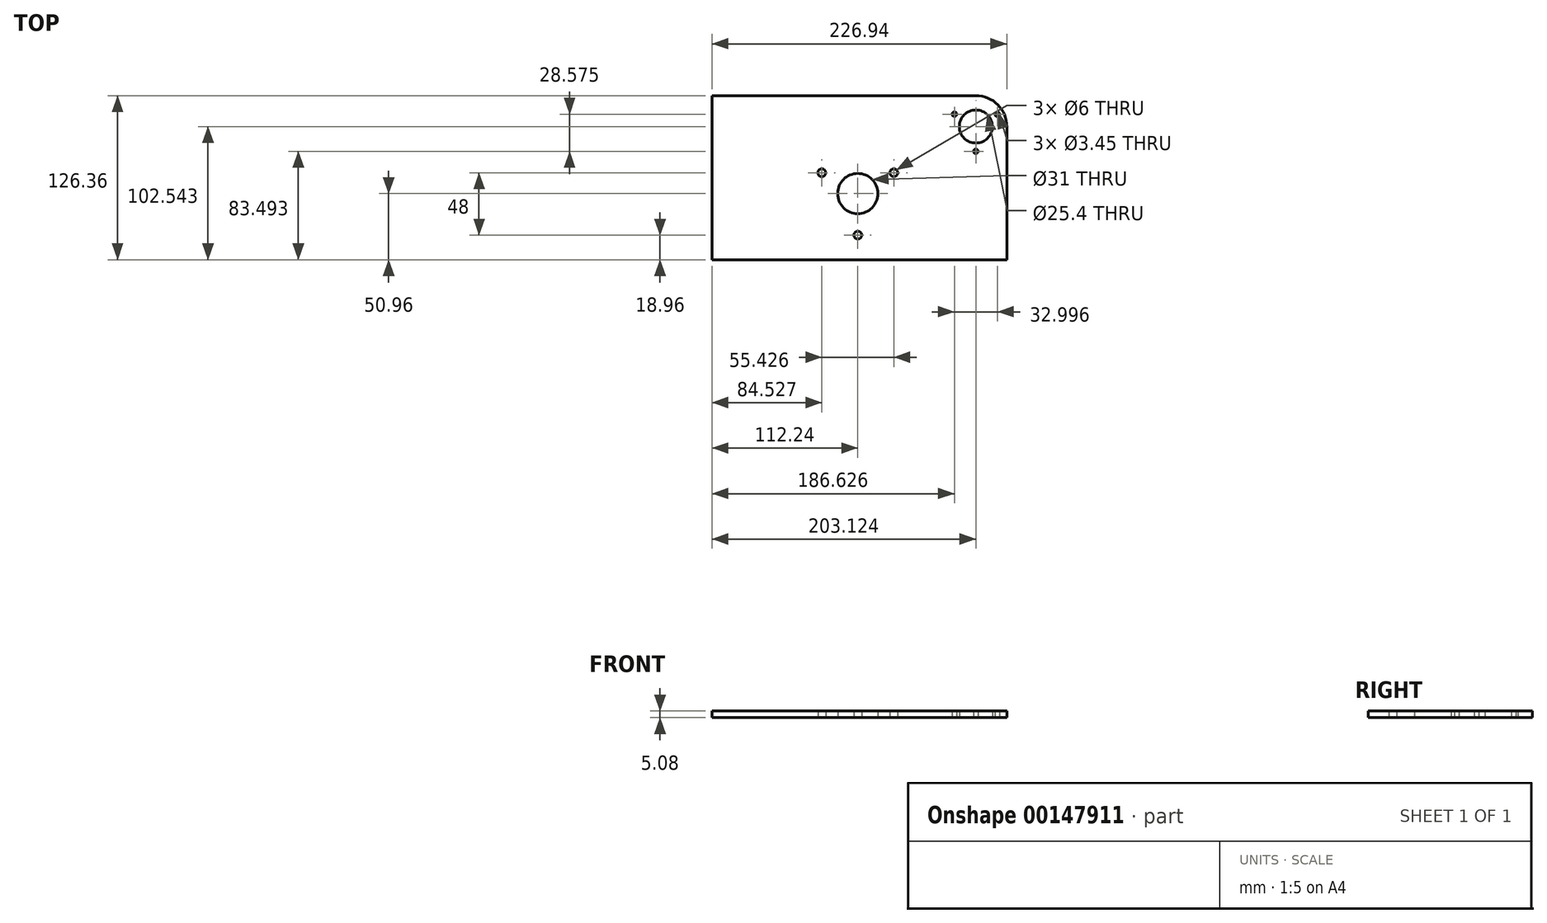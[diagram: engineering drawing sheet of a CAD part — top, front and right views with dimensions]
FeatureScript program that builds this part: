
annotation { "Feature Type Name" : "Feature", "Feature Type Description" : "" }
export const myFeature = defineFeature(function(context is Context, id is Id, definition is map)
    precondition{}
    {
        {
            var Q0;
            Q0=qCreatedBy(makeId("Top.planeOp"),FACE);
            var sketch = newSketch(context, id + "F0", { "sketchPlane" : qUnion([Q0])});
            skLineSegment(sketch, "E0", {"start": v(0, 0) * mm, "end": v(0, -32) * mm, "construction": true});
            skLineSegment(sketch, "E1", {"start": v(0, 0) * mm, "end": v(-27.71, 16) * mm, "construction": true});
            skLineSegment(sketch, "E2", {"start": v(0, 0) * mm, "end": v(27.71, 16) * mm, "construction": true});
            skLineSegment(sketch, "E3", {"start": v(0, -32) * mm, "end": v(-27.71, 16) * mm, "construction": true});
            skLineSegment(sketch, "E4", {"start": v(-27.71, 16) * mm, "end": v(27.71, 16) * mm, "construction": true});
            skLineSegment(sketch, "E5", {"start": v(27.71, 16) * mm, "end": v(0, -32) * mm, "construction": true});
            skCircle(sketch, "E6", {"center": v(0, 0) * mm, "radius": 15.5 * mm});
            skCircle(sketch, "E7", {"center": v(0, -32) * mm, "radius": 3 * mm});
            skCircle(sketch, "E8", {"center": v(27.71, 16) * mm, "radius": 3 * mm});
            skCircle(sketch, "E9", {"center": v(-27.71, 16) * mm, "radius": 3 * mm});
            skLineSegment(sketch, "E10", {"start": v(0, 0) * mm, "end": v(90.88, 0) * mm, "construction": true});
            skLineSegment(sketch, "E11", {"start": v(90.88, 0) * mm, "end": v(90.88, 51.58) * mm, "construction": true});
            skLineSegment(sketch, "E12", {"start": v(90.88, 51.58) * mm, "end": v(0, 0) * mm, "construction": true});
            skCircle(sketch, "E13", {"center": v(90.88, 51.58) * mm, "radius": 12.7 * mm});
            skCircle(sketch, "E14.cCircle", {"center": v(90.88, 51.58) * mm, "radius": 9.52 * mm, "construction": true});
            skLineSegment(sketch, "E14.0", {"start": v(74.39, 61.1) * mm, "end": v(107.38, 61.1) * mm, "construction": true});
            skLineSegment(sketch, "E14.1", {"start": v(107.38, 61.1) * mm, "end": v(90.88, 32.53) * mm, "construction": true});
            skLineSegment(sketch, "E14.2", {"start": v(90.88, 32.53) * mm, "end": v(74.39, 61.1) * mm, "construction": true});
            skPoint(sketch, "E14.0.midPoint", {"position": v(90.88, 61.1) * mm});
            skCircle(sketch, "E15", {"center": v(90.88, 51.58) * mm, "radius": 14.29 * mm, "construction": true});
            skCircle(sketch, "E16", {"center": v(74.39, 61.1) * mm, "radius": 4.76 * mm, "construction": true});
            skCircle(sketch, "E17", {"center": v(74.39, 61.1) * mm, "radius": 1.73 * mm});
            skCircle(sketch, "E18", {"center": v(107.38, 61.1) * mm, "radius": 1.73 * mm});
            skCircle(sketch, "E19", {"center": v(90.88, 32.53) * mm, "radius": 1.73 * mm});
            skLineSegment(sketch, "E20.bottom", {"start": v(-112.24, 75.4) * mm, "end": v(114.7, 75.4) * mm});
            skLineSegment(sketch, "E20.top", {"start": v(-112.24, -50.96) * mm, "end": v(114.7, -50.96) * mm});
            skLineSegment(sketch, "E20.left", {"start": v(-112.24, 75.4) * mm, "end": v(-112.24, -50.96) * mm});
            skLineSegment(sketch, "E20.right", {"start": v(114.7, 75.4) * mm, "end": v(114.7, -50.96) * mm});
            skCircle(sketch, "E21", {"center": v(90.88, 51.58) * mm, "radius": 23.81 * mm, "construction": true});
            skLineSegment(sketch, "E22", {"start": v(90.88, 0) * mm, "end": v(90.88, -50.96) * mm, "construction": true});
            skLineSegment(sketch, "E23", {"start": v(0, 0) * mm, "end": v(-112.24, 0) * mm, "construction": true});
            skSolve(sketch);
        }
        {
            var Q0;
            Q0=qSketchRegion(id+"F0",true);
            extrude(context, id + "F1", {"entities" : qUnion([Q0]), "depth" : 5.08 * mm});
        }
        {
            var Q0;
            Q0=makeQuery(id+"F1.opExtrude","SWEPT_EDGE",EDGE,{"disambiguationData":[OSD([sQuery(id+"F0.wireOp",EDGE,"E20.bottom"),sQuery(id+"F0.wireOp",EDGE,"E20.right")])]});
            fillet(context, id + "F2", {"entities" : qUnion([Q0]), "radius" : 23.8 * mm, "tangentPropagation" : true, "allowEdgeOverflow" : false});
        }
    });
